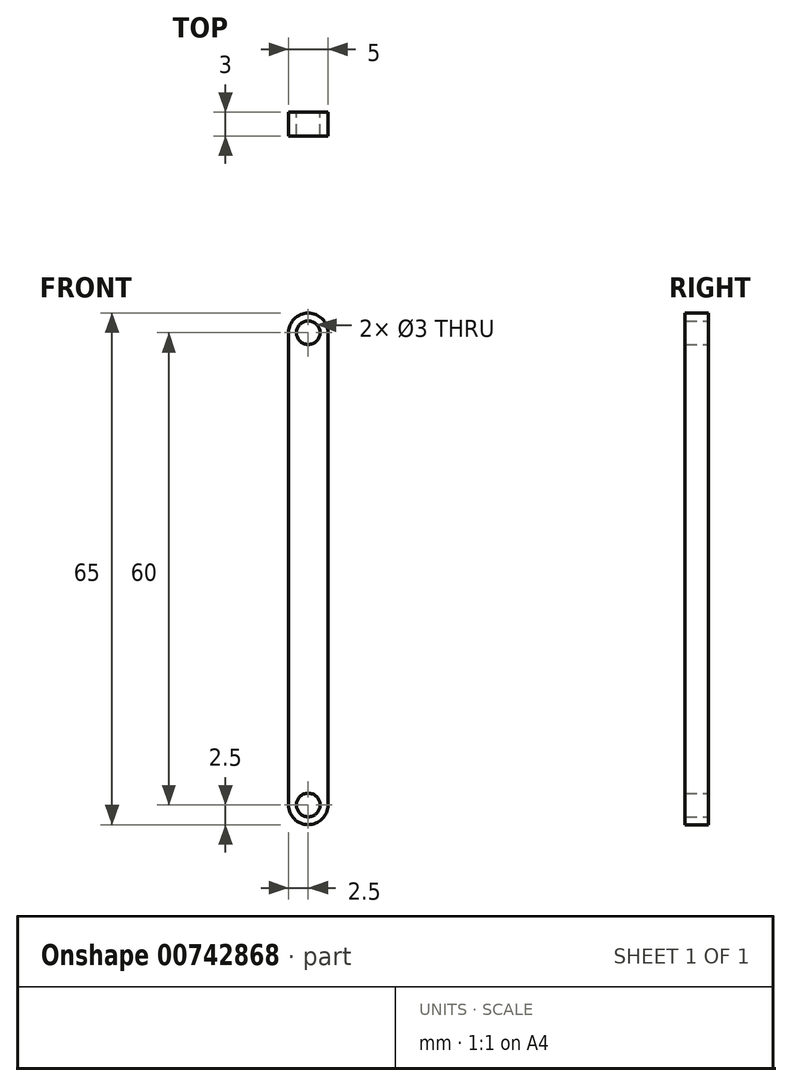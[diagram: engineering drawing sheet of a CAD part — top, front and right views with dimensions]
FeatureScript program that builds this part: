
annotation { "Feature Type Name" : "Feature", "Feature Type Description" : "" }
export const myFeature = defineFeature(function(context is Context, id is Id, definition is map)
    precondition{}
    {
        {
            var Q0;
            Q0=qCreatedBy(makeId("Front.planeOp"),FACE);
            var sketch = newSketch(context, id + "F0", { "sketchPlane" : qUnion([Q0])});
            skLineSegment(sketch, "E0.bottom", {"start": v(2.5, 30) * mm, "end": v(-2.5, 30) * mm, "construction": true});
            skLineSegment(sketch, "E0.top", {"start": v(2.5, -30) * mm, "end": v(-2.5, -30) * mm, "construction": true});
            skLineSegment(sketch, "E0.left", {"start": v(2.5, 30) * mm, "end": v(2.5, -30) * mm});
            skLineSegment(sketch, "E0.right", {"start": v(-2.5, 30) * mm, "end": v(-2.5, -30) * mm});
            skPoint(sketch, "E0.middle", {"position": v(0, 0) * mm});
            skArc(sketch, "E1", {"start": v(2.5, 30) * mm, "mid": v(0, 32.5) * mm, "end": v(-2.5, 30) * mm});
            skArc(sketch, "E2", {"start": v(-2.5, -30) * mm, "mid": v(0, -32.5) * mm, "end": v(2.5, -30) * mm});
            skCircle(sketch, "E3", {"center": v(0, 30) * mm, "radius": 1.5 * mm});
            skCircle(sketch, "E4", {"center": v(0, -30) * mm, "radius": 1.5 * mm});
            skSolve(sketch);
        }
        {
            var Q0;
            Q0 = qSketchRegion(id + "F0", true);
            extrude(context, id + "F1", {"entities" : qUnion([Q0]), "depth" : 3 * mm, "offsetDistance" : 25 * mm});
        }
    });
